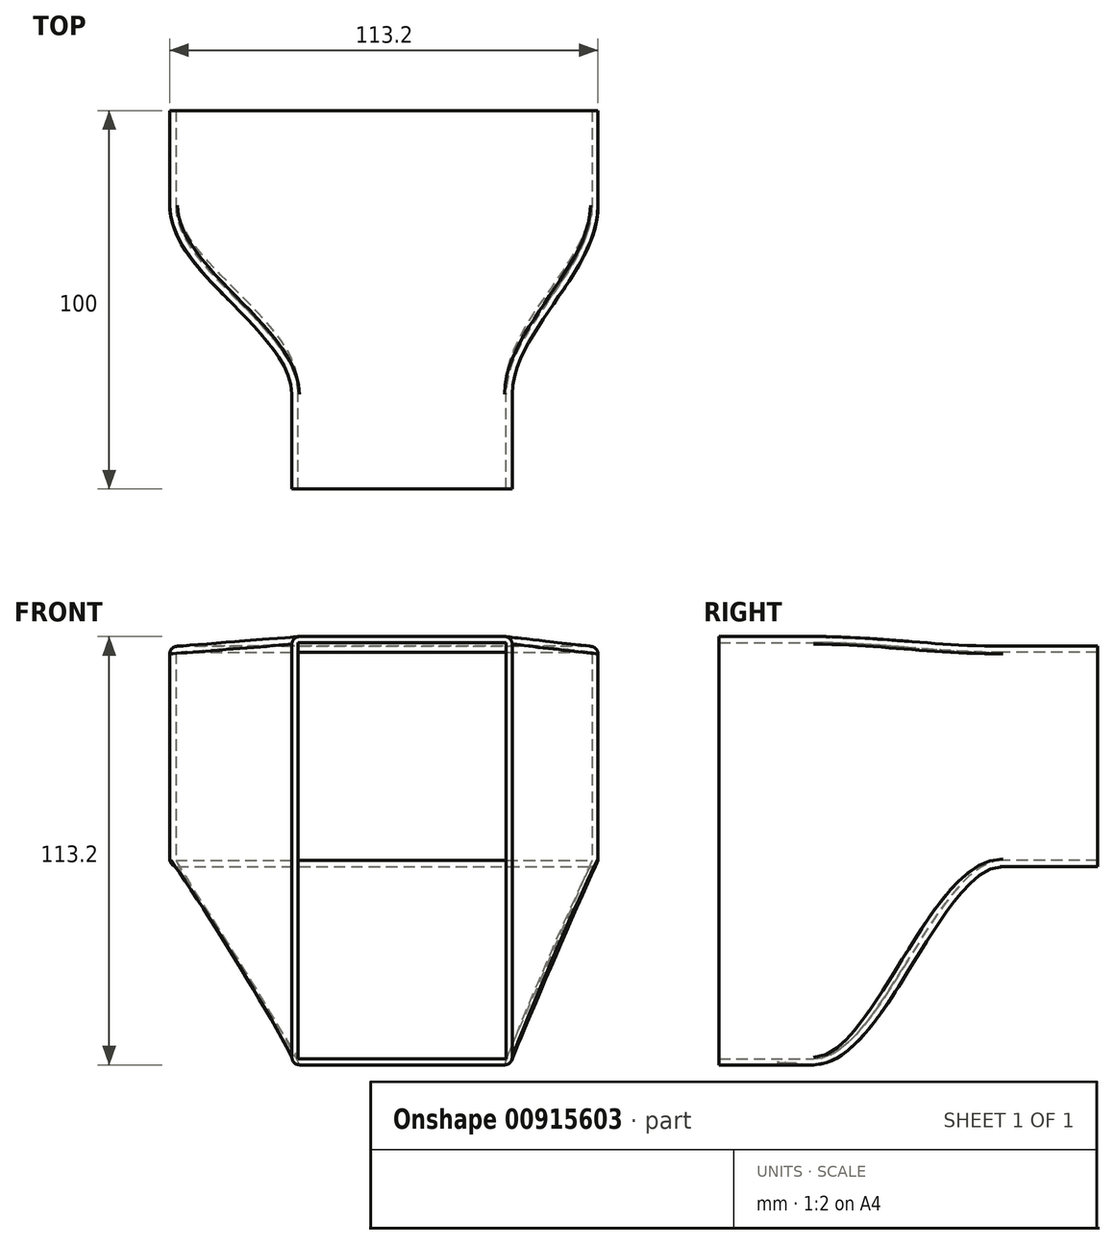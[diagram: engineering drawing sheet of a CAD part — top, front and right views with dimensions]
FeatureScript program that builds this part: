
annotation { "Feature Type Name" : "Feature", "Feature Type Description" : "" }
export const myFeature = defineFeature(function(context is Context, id is Id, definition is map)
    precondition{}
    {
        {
            var Q0;
            Q0=qCreatedBy(makeId("Front.planeOp"),FACE);
            var sketch = newSketch(context, id + "F0", { "sketchPlane" : qUnion([Q0])});
            skLineSegment(sketch, "E0.bottom", {"start": v(-56.1, 55.64) * mm, "end": v(53.9, 55.64) * mm});
            skLineSegment(sketch, "E0.top", {"start": v(-56.1, 0.64) * mm, "end": v(53.9, 0.64) * mm});
            skLineSegment(sketch, "E0.left", {"start": v(-56.1, 55.64) * mm, "end": v(-56.1, 0.64) * mm});
            skLineSegment(sketch, "E0.right", {"start": v(53.9, 55.64) * mm, "end": v(53.9, 0.64) * mm});
            skLineSegment(sketch, "E1.0", {"start": v(-57.7, 57.24) * mm, "end": v(55.5, 57.24) * mm});
            skLineSegment(sketch, "E1.1", {"start": v(-57.7, 57.24) * mm, "end": v(-57.7, -0.96) * mm});
            skLineSegment(sketch, "E1.2", {"start": v(-57.7, -0.96) * mm, "end": v(55.5, -0.96) * mm});
            skLineSegment(sketch, "E1.3", {"start": v(55.5, 57.24) * mm, "end": v(55.5, -0.96) * mm});
            skSolve(sketch);
        }
        {
            var Q0;
            Q0=qCreatedBy(makeId("Front.planeOp"),FACE);
            cPlane(context, id + "F1", {"entities" : qUnion([Q0]), "cplaneType" : CPlaneType.OFFSET, "offset" : 50 * mm, "width" : 150 * mm, "height" : 150 * mm});
        }
        {
            var Q0;
            Q0=qCreatedBy(id+"F1.planeOp",FACE);
            var sketch = newSketch(context, id + "F2", { "sketchPlane" : qUnion([Q0])});
            skLineSegment(sketch, "E2.bottom", {"start": v(-23.79, 58.21) * mm, "end": v(31.21, 58.21) * mm});
            skLineSegment(sketch, "E2.top", {"start": v(-23.79, -51.79) * mm, "end": v(31.21, -51.79) * mm});
            skLineSegment(sketch, "E2.left", {"start": v(-23.79, 58.21) * mm, "end": v(-23.79, -51.79) * mm});
            skLineSegment(sketch, "E2.right", {"start": v(31.21, 58.21) * mm, "end": v(31.21, -51.79) * mm});
            skLineSegment(sketch, "E3.0", {"start": v(-25.39, 59.81) * mm, "end": v(32.81, 59.81) * mm});
            skLineSegment(sketch, "E3.1", {"start": v(-25.39, 59.81) * mm, "end": v(-25.39, -53.39) * mm});
            skLineSegment(sketch, "E3.2", {"start": v(-25.39, -53.39) * mm, "end": v(32.81, -53.39) * mm});
            skLineSegment(sketch, "E3.3", {"start": v(32.81, 59.81) * mm, "end": v(32.81, -53.39) * mm});
            skSolve(sketch);
        }
        {
            var Q0;
            Q0=makeQuery(id+"F0.imprint","IMPRINT",FACE,{"disambiguationData":[TD([[makeQuery(id+"F0.imprint","IMPRINT",EDGE,{"derivedFrom":sQuery(id+"F0.wireOp",EDGE,"E0.bottom")}),-1.0]])]});
            var Q1;
            Q1=makeQuery(id+"F2.imprint","IMPRINT",FACE,{"disambiguationData":[TD([[makeQuery(id+"F2.imprint","IMPRINT",EDGE,{"derivedFrom":sQuery(id+"F2.wireOp",EDGE,"E2.bottom")}),-1.0]])]});
            loft(context, id + "F3", {"startCondition" : LoftEndDerivativeType.NORMAL_TO_PROFILE, "startMagnitude" : 1, "endCondition" : LoftEndDerivativeType.NORMAL_TO_PROFILE, "endMagnitude" : 1, "sheetProfilesArray" : [{ "sheetProfileEntities" : qUnion([Q0]) }, { "sheetProfileEntities" : qUnion([Q1]) }]});
        }
        {
            var Q0;
            Q0=makeQuery(id+"F3.opLoft","CAP_FACE",FACE,{"disambiguationData":[OSD([makeQuery(id+"F2.imprint","IMPRINT",FACE,{"disambiguationData":[TD([[makeQuery(id+"F2.imprint","IMPRINT",EDGE,{"derivedFrom":sQuery(id+"F2.wireOp",EDGE,"E2.bottom")}),-1.0]])]})])],"isStart":true});
            var Q1;
            Q1=makeQuery(id+"F3.opLoft","CAP_FACE",FACE,{"disambiguationData":[OSD([makeQuery(id+"F0.imprint","IMPRINT",FACE,{"disambiguationData":[TD([[makeQuery(id+"F0.imprint","IMPRINT",EDGE,{"derivedFrom":sQuery(id+"F0.wireOp",EDGE,"E0.bottom")}),-1.0]])]})])],"isStart":true});
            shell(context, id + "F4", {"entities" : qUnion([Q0, Q1]), "thickness" : 1.6 * mm, "oppositeDirection" : true});
        }
        {
            var Q0;
            Q0 = qSketchRegion(id + "F2", true);
            extrude(context, id + "F5", {"entities" : qUnion([Q0]), "operationType" : NewBodyOperationType.ADD, "depth" : 25 * mm, "offsetDistance" : 25 * mm});
        }
        {
            var Q0;
            Q0 = qSketchRegion(id + "F0", true);
            extrude(context, id + "F6", {"entities" : qUnion([Q0]), "operationType" : NewBodyOperationType.ADD, "oppositeDirection" : true, "depth" : 25 * mm, "offsetDistance" : 25 * mm});
        }
        {
            var Q0;
            Q0=makeQuery(id+"F6.opExtrude","SWEPT_EDGE",EDGE,{"disambiguationData":[OSD([sQuery(id+"F0.wireOp",EDGE,"E1.0"),sQuery(id+"F0.wireOp",EDGE,"E1.3")])]});
            var Q1;
            Q1=makeQuery(id+"F6.opExtrude","SWEPT_EDGE",EDGE,{"disambiguationData":[OSD([sQuery(id+"F0.wireOp",EDGE,"E1.0"),sQuery(id+"F0.wireOp",EDGE,"E1.1")])]});
            var Q2;
            Q2=makeQuery(id+"F6.opExtrude","SWEPT_EDGE",EDGE,{"disambiguationData":[OSD([sQuery(id+"F0.wireOp",EDGE,"E1.2"),sQuery(id+"F0.wireOp",EDGE,"E1.3")])]});
            var Q3;
            Q3=makeQuery(id+"F6.opExtrude","SWEPT_EDGE",EDGE,{"disambiguationData":[OSD([sQuery(id+"F0.wireOp",EDGE,"E1.1"),sQuery(id+"F0.wireOp",EDGE,"E1.2")])]});
            fillet(context, id + "F7", {"entities" : qUnion([Q0, Q1, Q2, Q3]), "radius" : 2 * mm, "tangentPropagation" : true, "allowEdgeOverflow" : false});
        }
    });
